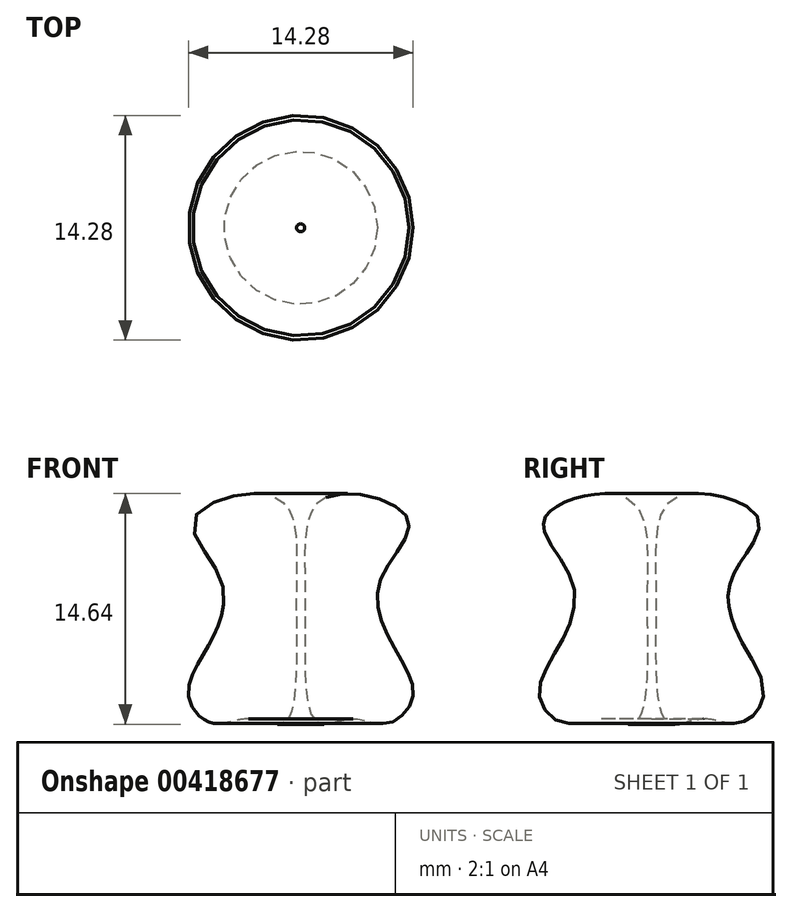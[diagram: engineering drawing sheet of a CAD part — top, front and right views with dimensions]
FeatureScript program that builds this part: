
annotation { "Feature Type Name" : "Feature", "Feature Type Description" : "" }
export const myFeature = defineFeature(function(context is Context, id is Id, definition is map)
    precondition{}
    {
        {
            var Q0;
            Q0=qCreatedBy(makeId("Front.planeOp"),FACE);
            var sketch = newSketch(context, id + "F0", { "sketchPlane" : qUnion([Q0])});
            skFitSpline(sketch, "E0", {"points": [v(1.34, 6.05) * mm, v(0, 0) * mm, v(0.73, -8.23) * mm, v(2.9, -8.03) * mm, v(5.29, -8.3) * mm, v(6.85, -6.53) * mm, v(5.49, -3.2) * mm, v(4.8, 0.88) * mm, v(6.5, 4.69) * mm, v(1.34, 6.05) * mm]});
            skLineSegment(sketch, "E1", {"start": v(-0.28, 3.73) * mm, "end": v(-0.28, 4.68) * mm});
            skSolve(sketch);
        }
        {
            var Q0;
            Q0 = qSketchRegion(id + "F0", true);
            var Q1;
            Q1=sQuery(id+"F0.wireOp",EDGE,"E1");
            revolve(context, id + "F1", {"surfaceOperationType" : NewSurfaceOperationType.NEW, "entities" : qUnion([Q0]), "axis" : qUnion([Q1]), "revolveType" : RevolveType.FULL});
        }
    });
